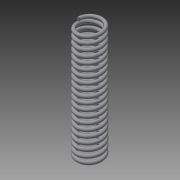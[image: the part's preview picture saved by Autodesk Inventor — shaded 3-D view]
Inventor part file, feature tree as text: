
AUTODESK INVENTOR PART (.ipt)
format: ipt  version: 2014 SP1 (Build 180222100, 222)  size: 876,032 bytes
history: native  units: in
note: dims shown in document units (in); Inventor stores cm internally (conversion verified against a paired STEP export)
features: other x1, helix x1, sketch x1
ambient origin geometry x8: Origin, YZ Plane, XZ Plane, XY Plane, X Axis, Y Axis, Z Axis, Center Point
bodies: Solid1 (feature_tree)
feature tree (3):
  other  "Large Mainspring"
  helix  "Coil1"  [1 undecoded]
  sketch  "Sketch1"  dims[d1=0.032in d2=1.068in d3=1.036in d4=1.0in d5=1.036in d6=7.4803in d7=0.0in d8=90.0deg d9=90.0deg d10=90.0deg d11=90.0deg]
note: 1 required parameter value undecoded (feature->parameter linkage not recoverable at this tier; creation-order binding heuristic only, values carry confidence <= 0.55)
